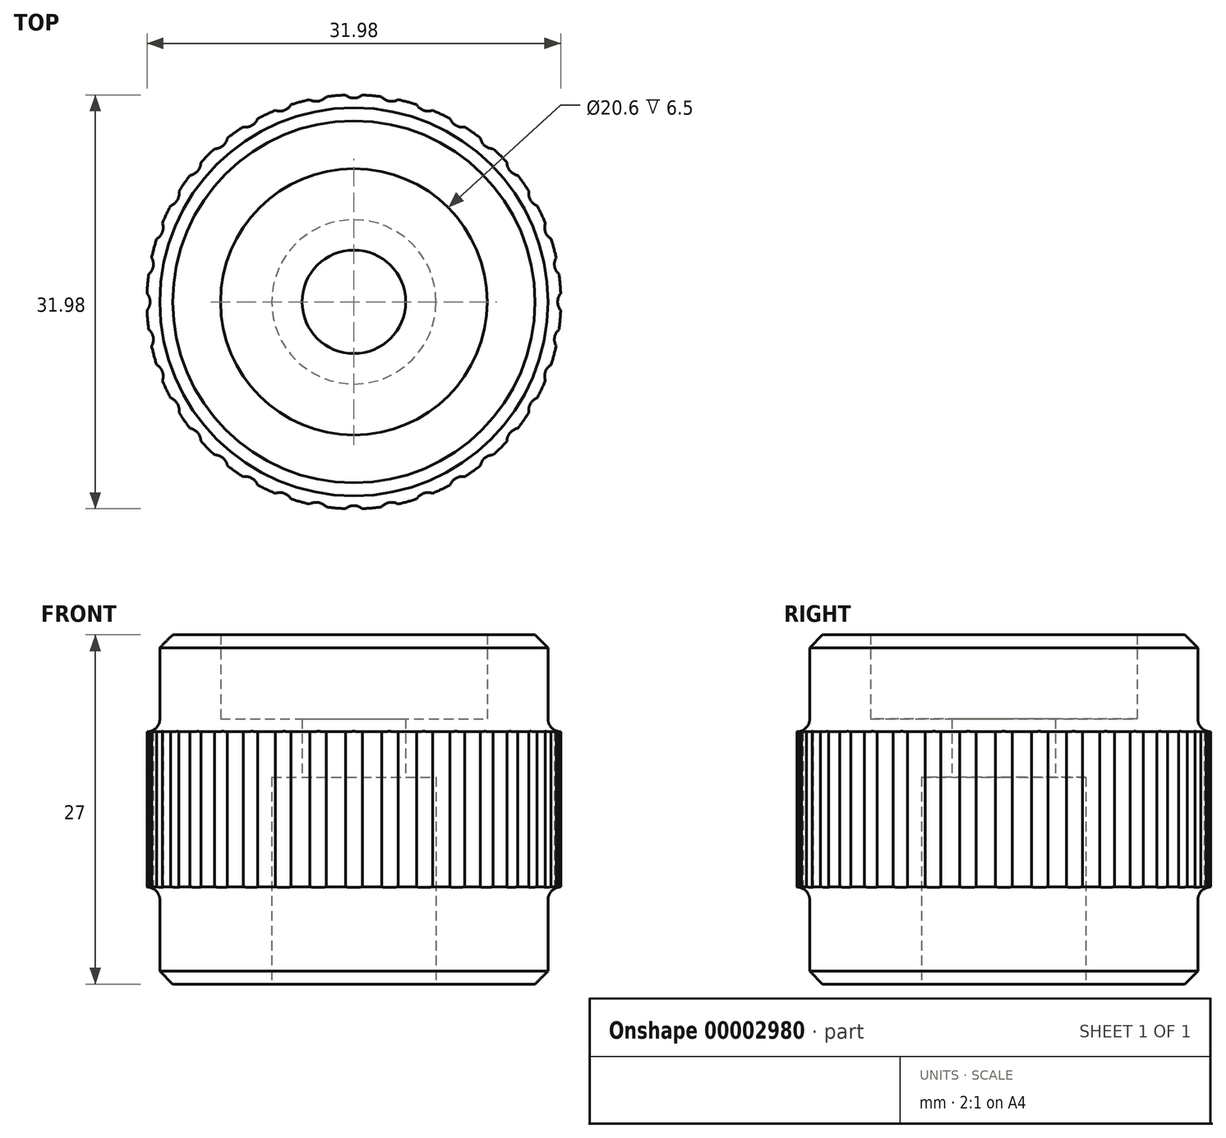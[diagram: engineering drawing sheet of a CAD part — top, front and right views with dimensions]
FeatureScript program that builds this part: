
annotation { "Feature Type Name" : "Feature", "Feature Type Description" : "" }
export const myFeature = defineFeature(function(context is Context, id is Id, definition is map)
    precondition{}
    {
        {
            var Q0;
            Q0=qCreatedBy(makeId("Front.planeOp"),FACE);
            var sketch = newSketch(context, id + "F0", { "sketchPlane" : qUnion([Q0])});
            skLineSegment(sketch, "E0", {"start": v(-6.35, -6.19) * mm, "end": v(-6.35, 9.81) * mm});
            skLineSegment(sketch, "E1", {"start": v(-6.35, 9.81) * mm, "end": v(-4, 9.81) * mm});
            skLineSegment(sketch, "E2", {"start": v(-4, 9.81) * mm, "end": v(-4, 14.31) * mm});
            skLineSegment(sketch, "E3", {"start": v(-4, 14.31) * mm, "end": v(-10.3, 14.31) * mm});
            skLineSegment(sketch, "E4", {"start": v(-10.3, 14.31) * mm, "end": v(-10.3, 20.81) * mm});
            skLineSegment(sketch, "E5", {"start": v(-10.3, 20.81) * mm, "end": v(-15, 20.81) * mm});
            skLineSegment(sketch, "E6", {"start": v(-15, 20.81) * mm, "end": v(-15, 13.31) * mm});
            skLineSegment(sketch, "E7", {"start": v(-15, -6.19) * mm, "end": v(-6.35, -6.19) * mm});
            skLineSegment(sketch, "E8", {"start": v(0, 0) * mm, "end": v(0, 42.19) * mm, "construction": true});
            skLineSegment(sketch, "E9", {"start": v(-15, 13.31) * mm, "end": v(-16, 13.31) * mm});
            skLineSegment(sketch, "E10", {"start": v(-16, 13.31) * mm, "end": v(-16, 1.31) * mm});
            skLineSegment(sketch, "E11", {"start": v(-16, 1.31) * mm, "end": v(-15, 1.31) * mm});
            skLineSegment(sketch, "E12.trimOffspring", {"start": v(-15, 1.31) * mm, "end": v(-15, -6.19) * mm});
            skLineSegment(sketch, "E13", {"start": v(0, 0) * mm, "end": v(0, -37.87) * mm, "construction": true});
            skSolve(sketch);
        }
        {
            var Q0;
            Q0=makeQuery(id+"F0.imprint","IMPRINT",FACE,{"disambiguationData":[TD([[makeQuery(id+"F0.imprint","IMPRINT",EDGE,{"derivedFrom":sQuery(id+"F0.wireOp",EDGE,"E0")}),1.0]])]});
            var Q1;
            Q1=sQuery(id+"F0.wireOp",EDGE,"E8");
            revolve(context, id + "F1", {"entities" : qUnion([Q0]), "axis" : qUnion([Q1]), "revolveType" : RevolveType.FULL});
        }
        {
            var Q0;
            Q0=makeQuery(id+"F1.opRevolve","SWEPT_EDGE",EDGE,{"disambiguationData":[OSD([sQuery(id+"F0.wireOp",EDGE,"E5"),sQuery(id+"F0.wireOp",EDGE,"E6")])]});
            var Q1;
            Q1=makeQuery(id+"F1.opRevolve","SWEPT_EDGE",EDGE,{"disambiguationData":[OSD([sQuery(id+"F0.wireOp",EDGE,"E7"),sQuery(id+"F0.wireOp",EDGE,"E12.trimOffspring")])]});
            chamfer(context, id + "F2", {"entities" : qUnion([Q0, Q1]), "width" : 1 * mm, "tangentPropagation" : true});
        }
        {
            var Q0;
            Q0=makeQuery(id+"F1.opRevolve","SWEPT_EDGE",EDGE,{"disambiguationData":[OSD([sQuery(id+"F0.wireOp",EDGE,"E6"),sQuery(id+"F0.wireOp",EDGE,"E9")])]});
            var Q1;
            Q1=makeQuery(id+"F1.opRevolve","SWEPT_EDGE",EDGE,{"disambiguationData":[OSD([sQuery(id+"F0.wireOp",EDGE,"E11"),sQuery(id+"F0.wireOp",EDGE,"E12.trimOffspring")])]});
            fillet(context, id + "F3", {"entities" : qUnion([Q0, Q1]), "radius" : 1 * mm, "tangentPropagation" : true, "allowEdgeOverflow" : false});
        }
        {
            var Q0;
            Q0=qCreatedBy(makeId("Top.planeOp"),FACE);
            var sketch = newSketch(context, id + "F4", { "sketchPlane" : qUnion([Q0])});
            skLineSegment(sketch, "E14", {"start": v(0, 0) * mm, "end": v(0, 16.75) * mm, "construction": true});
            skCircle(sketch, "E15", {"center": v(0, 16.75) * mm, "radius": 1 * mm});
            skSolve(sketch);
        }
        {
            var Q0;
            Q0=makeQuery(id+"F4.imprint","IMPRINT",FACE,{"disambiguationData":[TD([[makeQuery(id+"F4.imprint","IMPRINT",EDGE,{"derivedFrom":sQuery(id+"F4.wireOp",EDGE,"E15")}),1.0]])]});
            extrude(context, id + "F5", {"entities" : qUnion([Q0]), "depth" : 15 * mm});
        }
        {
            var Q0;
            Q0=makeQuery(id+"F5.opExtrude","SWEPT_BODY",BODY,{"disambiguationData":[OSD([sQuery(id+"F4.wireOp",EDGE,"E15")])]});
            var Q1;
            Q1=sQuery(id+"F0.wireOp",EDGE,"E13");
            circularPattern(context, id + "F6", {"entities" : qUnion([Q0]), "axis" : qUnion([Q1]), "angle" : 10 * degree, "instanceCount" : 36});
        }
        {
            var Q0;
            Q0=makeQuery(id+"F6.opPattern","COPY",BODY,{"derivedFrom":makeQuery(id+"F5.opExtrude","SWEPT_BODY",BODY,{"disambiguationData":[OSD([sQuery(id+"F4.wireOp",EDGE,"E15")])]}),"instanceName":"3"});
            var Q1;
            Q1=makeQuery(id+"F6.opPattern","COPY",BODY,{"derivedFrom":makeQuery(id+"F5.opExtrude","SWEPT_BODY",BODY,{"disambiguationData":[OSD([sQuery(id+"F4.wireOp",EDGE,"E15")])]}),"instanceName":"16"});
            var Q2;
            Q2=makeQuery(id+"F6.opPattern","COPY",BODY,{"derivedFrom":makeQuery(id+"F5.opExtrude","SWEPT_BODY",BODY,{"disambiguationData":[OSD([sQuery(id+"F4.wireOp",EDGE,"E15")])]}),"instanceName":"34"});
            var Q3;
            Q3=makeQuery(id+"F6.opPattern","COPY",BODY,{"derivedFrom":makeQuery(id+"F5.opExtrude","SWEPT_BODY",BODY,{"disambiguationData":[OSD([sQuery(id+"F4.wireOp",EDGE,"E15")])]}),"instanceName":"14"});
            var Q4;
            Q4=makeQuery(id+"F6.opPattern","COPY",BODY,{"derivedFrom":makeQuery(id+"F5.opExtrude","SWEPT_BODY",BODY,{"disambiguationData":[OSD([sQuery(id+"F4.wireOp",EDGE,"E15")])]}),"instanceName":"23"});
            var Q5;
            Q5=makeQuery(id+"F6.opPattern","COPY",BODY,{"derivedFrom":makeQuery(id+"F5.opExtrude","SWEPT_BODY",BODY,{"disambiguationData":[OSD([sQuery(id+"F4.wireOp",EDGE,"E15")])]}),"instanceName":"7"});
            var Q6;
            Q6=makeQuery(id+"F6.opPattern","COPY",BODY,{"derivedFrom":makeQuery(id+"F5.opExtrude","SWEPT_BODY",BODY,{"disambiguationData":[OSD([sQuery(id+"F4.wireOp",EDGE,"E15")])]}),"instanceName":"8"});
            var Q7;
            Q7=makeQuery(id+"F6.opPattern","COPY",BODY,{"derivedFrom":makeQuery(id+"F5.opExtrude","SWEPT_BODY",BODY,{"disambiguationData":[OSD([sQuery(id+"F4.wireOp",EDGE,"E15")])]}),"instanceName":"18"});
            var Q8;
            Q8=makeQuery(id+"F6.opPattern","COPY",BODY,{"derivedFrom":makeQuery(id+"F5.opExtrude","SWEPT_BODY",BODY,{"disambiguationData":[OSD([sQuery(id+"F4.wireOp",EDGE,"E15")])]}),"instanceName":"17"});
            var Q9;
            Q9=makeQuery(id+"F6.opPattern","COPY",BODY,{"derivedFrom":makeQuery(id+"F5.opExtrude","SWEPT_BODY",BODY,{"disambiguationData":[OSD([sQuery(id+"F4.wireOp",EDGE,"E15")])]}),"instanceName":"9"});
            var Q10;
            Q10=makeQuery(id+"F6.opPattern","COPY",BODY,{"derivedFrom":makeQuery(id+"F5.opExtrude","SWEPT_BODY",BODY,{"disambiguationData":[OSD([sQuery(id+"F4.wireOp",EDGE,"E15")])]}),"instanceName":"15"});
            var Q11;
            Q11=makeQuery(id+"F6.opPattern","COPY",BODY,{"derivedFrom":makeQuery(id+"F5.opExtrude","SWEPT_BODY",BODY,{"disambiguationData":[OSD([sQuery(id+"F4.wireOp",EDGE,"E15")])]}),"instanceName":"12"});
            var Q12;
            Q12=makeQuery(id+"F6.opPattern","COPY",BODY,{"derivedFrom":makeQuery(id+"F5.opExtrude","SWEPT_BODY",BODY,{"disambiguationData":[OSD([sQuery(id+"F4.wireOp",EDGE,"E15")])]}),"instanceName":"28"});
            var Q13;
            Q13=makeQuery(id+"F6.opPattern","COPY",BODY,{"derivedFrom":makeQuery(id+"F5.opExtrude","SWEPT_BODY",BODY,{"disambiguationData":[OSD([sQuery(id+"F4.wireOp",EDGE,"E15")])]}),"instanceName":"24"});
            var Q14;
            Q14=makeQuery(id+"F6.opPattern","COPY",BODY,{"derivedFrom":makeQuery(id+"F5.opExtrude","SWEPT_BODY",BODY,{"disambiguationData":[OSD([sQuery(id+"F4.wireOp",EDGE,"E15")])]}),"instanceName":"30"});
            var Q15;
            Q15=makeQuery(id+"F6.opPattern","COPY",BODY,{"derivedFrom":makeQuery(id+"F5.opExtrude","SWEPT_BODY",BODY,{"disambiguationData":[OSD([sQuery(id+"F4.wireOp",EDGE,"E15")])]}),"instanceName":"31"});
            var Q16;
            Q16=makeQuery(id+"F6.opPattern","COPY",BODY,{"derivedFrom":makeQuery(id+"F5.opExtrude","SWEPT_BODY",BODY,{"disambiguationData":[OSD([sQuery(id+"F4.wireOp",EDGE,"E15")])]}),"instanceName":"25"});
            var Q17;
            Q17=makeQuery(id+"F6.opPattern","COPY",BODY,{"derivedFrom":makeQuery(id+"F5.opExtrude","SWEPT_BODY",BODY,{"disambiguationData":[OSD([sQuery(id+"F4.wireOp",EDGE,"E15")])]}),"instanceName":"21"});
            var Q18;
            Q18=makeQuery(id+"F6.opPattern","COPY",BODY,{"derivedFrom":makeQuery(id+"F5.opExtrude","SWEPT_BODY",BODY,{"disambiguationData":[OSD([sQuery(id+"F4.wireOp",EDGE,"E15")])]}),"instanceName":"4"});
            var Q19;
            Q19=makeQuery(id+"F6.opPattern","COPY",BODY,{"derivedFrom":makeQuery(id+"F5.opExtrude","SWEPT_BODY",BODY,{"disambiguationData":[OSD([sQuery(id+"F4.wireOp",EDGE,"E15")])]}),"instanceName":"5"});
            var Q20;
            Q20=makeQuery(id+"F6.opPattern","COPY",BODY,{"derivedFrom":makeQuery(id+"F5.opExtrude","SWEPT_BODY",BODY,{"disambiguationData":[OSD([sQuery(id+"F4.wireOp",EDGE,"E15")])]}),"instanceName":"11"});
            var Q21;
            Q21=makeQuery(id+"F6.opPattern","COPY",BODY,{"derivedFrom":makeQuery(id+"F5.opExtrude","SWEPT_BODY",BODY,{"disambiguationData":[OSD([sQuery(id+"F4.wireOp",EDGE,"E15")])]}),"instanceName":"1"});
            var Q22;
            Q22=makeQuery(id+"F6.opPattern","COPY",BODY,{"derivedFrom":makeQuery(id+"F5.opExtrude","SWEPT_BODY",BODY,{"disambiguationData":[OSD([sQuery(id+"F4.wireOp",EDGE,"E15")])]}),"instanceName":"29"});
            var Q23;
            Q23=makeQuery(id+"F6.opPattern","COPY",BODY,{"derivedFrom":makeQuery(id+"F5.opExtrude","SWEPT_BODY",BODY,{"disambiguationData":[OSD([sQuery(id+"F4.wireOp",EDGE,"E15")])]}),"instanceName":"20"});
            var Q24;
            Q24=makeQuery(id+"F6.opPattern","COPY",BODY,{"derivedFrom":makeQuery(id+"F5.opExtrude","SWEPT_BODY",BODY,{"disambiguationData":[OSD([sQuery(id+"F4.wireOp",EDGE,"E15")])]}),"instanceName":"13"});
            var Q25;
            Q25=makeQuery(id+"F6.opPattern","COPY",BODY,{"derivedFrom":makeQuery(id+"F5.opExtrude","SWEPT_BODY",BODY,{"disambiguationData":[OSD([sQuery(id+"F4.wireOp",EDGE,"E15")])]}),"instanceName":"19"});
            var Q26;
            Q26=makeQuery(id+"F6.opPattern","COPY",BODY,{"derivedFrom":makeQuery(id+"F5.opExtrude","SWEPT_BODY",BODY,{"disambiguationData":[OSD([sQuery(id+"F4.wireOp",EDGE,"E15")])]}),"instanceName":"22"});
            var Q27;
            Q27=makeQuery(id+"F6.opPattern","COPY",BODY,{"derivedFrom":makeQuery(id+"F5.opExtrude","SWEPT_BODY",BODY,{"disambiguationData":[OSD([sQuery(id+"F4.wireOp",EDGE,"E15")])]}),"instanceName":"32"});
            var Q28;
            Q28=makeQuery(id+"F6.opPattern","COPY",BODY,{"derivedFrom":makeQuery(id+"F5.opExtrude","SWEPT_BODY",BODY,{"disambiguationData":[OSD([sQuery(id+"F4.wireOp",EDGE,"E15")])]}),"instanceName":"26"});
            var Q29;
            Q29=makeQuery(id+"F6.opPattern","COPY",BODY,{"derivedFrom":makeQuery(id+"F5.opExtrude","SWEPT_BODY",BODY,{"disambiguationData":[OSD([sQuery(id+"F4.wireOp",EDGE,"E15")])]}),"instanceName":"10"});
            var Q30;
            Q30=makeQuery(id+"F6.opPattern","COPY",BODY,{"derivedFrom":makeQuery(id+"F5.opExtrude","SWEPT_BODY",BODY,{"disambiguationData":[OSD([sQuery(id+"F4.wireOp",EDGE,"E15")])]}),"instanceName":"27"});
            var Q31;
            Q31=makeQuery(id+"F6.opPattern","COPY",BODY,{"derivedFrom":makeQuery(id+"F5.opExtrude","SWEPT_BODY",BODY,{"disambiguationData":[OSD([sQuery(id+"F4.wireOp",EDGE,"E15")])]}),"instanceName":"2"});
            var Q32;
            Q32=makeQuery(id+"F5.opExtrude","SWEPT_BODY",BODY,{"disambiguationData":[OSD([sQuery(id+"F4.wireOp",EDGE,"E15")])]});
            var Q33;
            Q33=makeQuery(id+"F6.opPattern","COPY",BODY,{"derivedFrom":makeQuery(id+"F5.opExtrude","SWEPT_BODY",BODY,{"disambiguationData":[OSD([sQuery(id+"F4.wireOp",EDGE,"E15")])]}),"instanceName":"6"});
            var Q34;
            Q34=makeQuery(id+"F6.opPattern","COPY",BODY,{"derivedFrom":makeQuery(id+"F5.opExtrude","SWEPT_BODY",BODY,{"disambiguationData":[OSD([sQuery(id+"F4.wireOp",EDGE,"E15")])]}),"instanceName":"33"});
            var Q35;
            Q35=makeQuery(id+"F6.opPattern","COPY",BODY,{"derivedFrom":makeQuery(id+"F5.opExtrude","SWEPT_BODY",BODY,{"disambiguationData":[OSD([sQuery(id+"F4.wireOp",EDGE,"E15")])]}),"instanceName":"35"});
            var Q36;
            Q36=makeQuery(id+"F1.opRevolve","SWEPT_BODY",BODY,{"disambiguationData":[OSD([sQuery(id+"F0.wireOp",EDGE,"E0"),sQuery(id+"F0.wireOp",EDGE,"E1"),sQuery(id+"F0.wireOp",EDGE,"E2"),sQuery(id+"F0.wireOp",EDGE,"E3"),sQuery(id+"F0.wireOp",EDGE,"E4"),sQuery(id+"F0.wireOp",EDGE,"E5"),sQuery(id+"F0.wireOp",EDGE,"E6"),sQuery(id+"F0.wireOp",EDGE,"E7"),sQuery(id+"F0.wireOp",EDGE,"E9"),sQuery(id+"F0.wireOp",EDGE,"E10"),sQuery(id+"F0.wireOp",EDGE,"E11"),sQuery(id+"F0.wireOp",EDGE,"E12.trimOffspring")])]});
            booleanBodies(context, id + "F7", {"operationType" : BooleanOperationType.SUBTRACTION, "tools" : qUnion([Q0, Q1, Q2, Q3, Q4, Q5, Q6, Q7, Q8, Q9, Q10, Q11, Q12, Q13, Q14, Q15, Q16, Q17, Q18, Q19, Q20, Q21, Q22, Q23, Q24, Q25, Q26, Q27, Q28, Q29, Q30, Q31, Q32, Q33, Q34, Q35]), "targets" : qUnion([Q36])});
        }
    });
